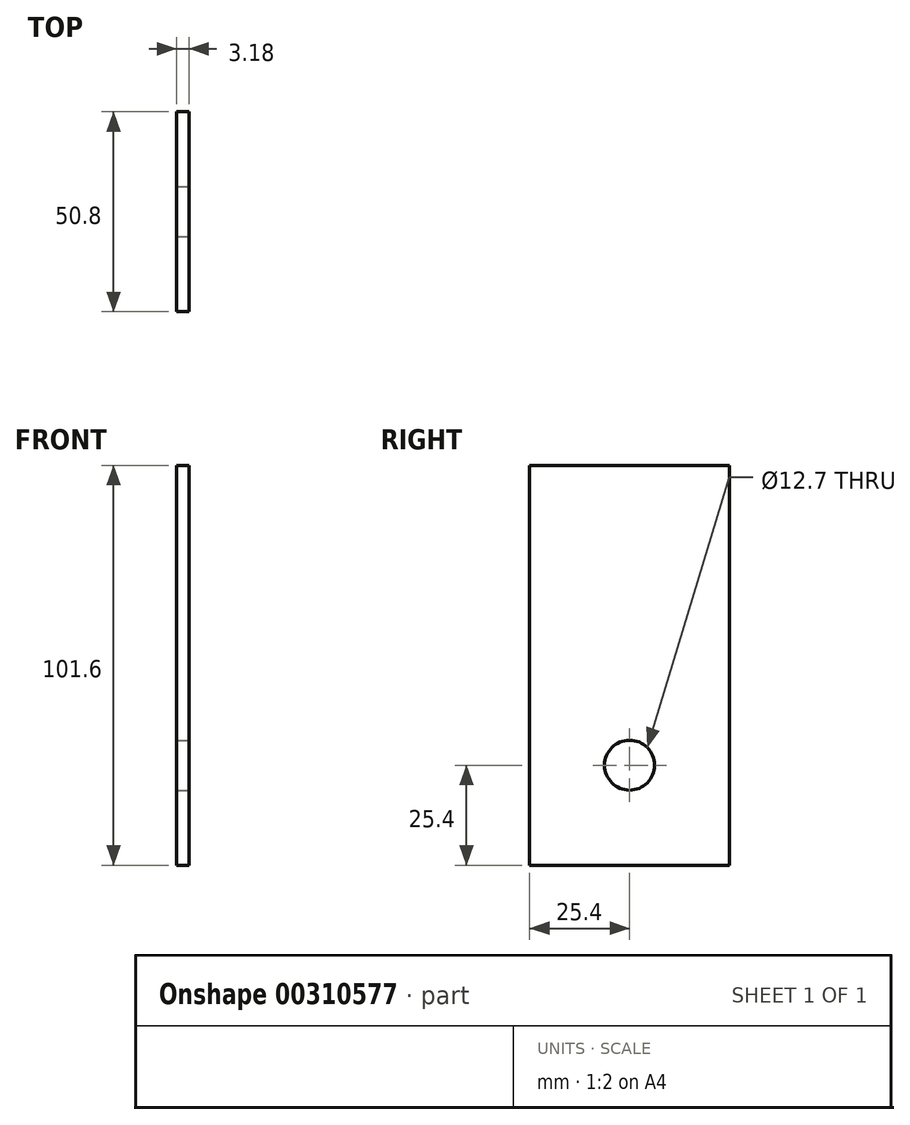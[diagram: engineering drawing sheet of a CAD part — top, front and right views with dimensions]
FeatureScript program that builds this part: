
annotation { "Feature Type Name" : "Feature", "Feature Type Description" : "" }
export const myFeature = defineFeature(function(context is Context, id is Id, definition is map)
    precondition{}
    {
        {
            var Q0;
            Q0=qCreatedBy(makeId("Front.planeOp"),FACE);
            var sketch = newSketch(context, id + "F0", { "sketchPlane" : qUnion([Q0])});
            skLineSegment(sketch, "E0", {"start": v(0, 0) * mm, "end": v(0, 101.6) * mm});
            skLineSegment(sketch, "E1", {"start": v(0, 101.6) * mm, "end": v(3.17, 101.6) * mm});
            skLineSegment(sketch, "E2", {"start": v(3.17, 101.6) * mm, "end": v(3.18, 0) * mm});
            skLineSegment(sketch, "E3", {"start": v(0, 0) * mm, "end": v(3.18, 0) * mm});
            skSolve(sketch);
        }
        {
            var Q0;
            Q0 = qSketchRegion(id + "F0", true);
            extrude(context, id + "F1", {"entities" : qUnion([Q0]), "depth" : 50.8 * mm});
        }
        {
            var Q0;
            Q0=makeQuery(id+"F1.opExtrude","SWEPT_FACE",FACE,{"disambiguationData":[OSD([sQuery(id+"F0.wireOp",EDGE,"E2")])]});
            var sketch = newSketch(context, id + "F2", { "sketchPlane" : qUnion([Q0])});
            skCircle(sketch, "E4", {"center": v(-25.4, 25.4) * mm, "radius": 6.35 * mm});
            skSolve(sketch);
        }
        {
            var Q0;
            Q0 = qSketchRegion(id + "F2", true);
            extrude(context, id + "F3", {"entities" : qUnion([Q0]), "operationType" : NewBodyOperationType.REMOVE, "endBound" : BoundingType.THROUGH_ALL, "oppositeDirection" : true, "depth" : 25.4 * mm});
        }
    });
